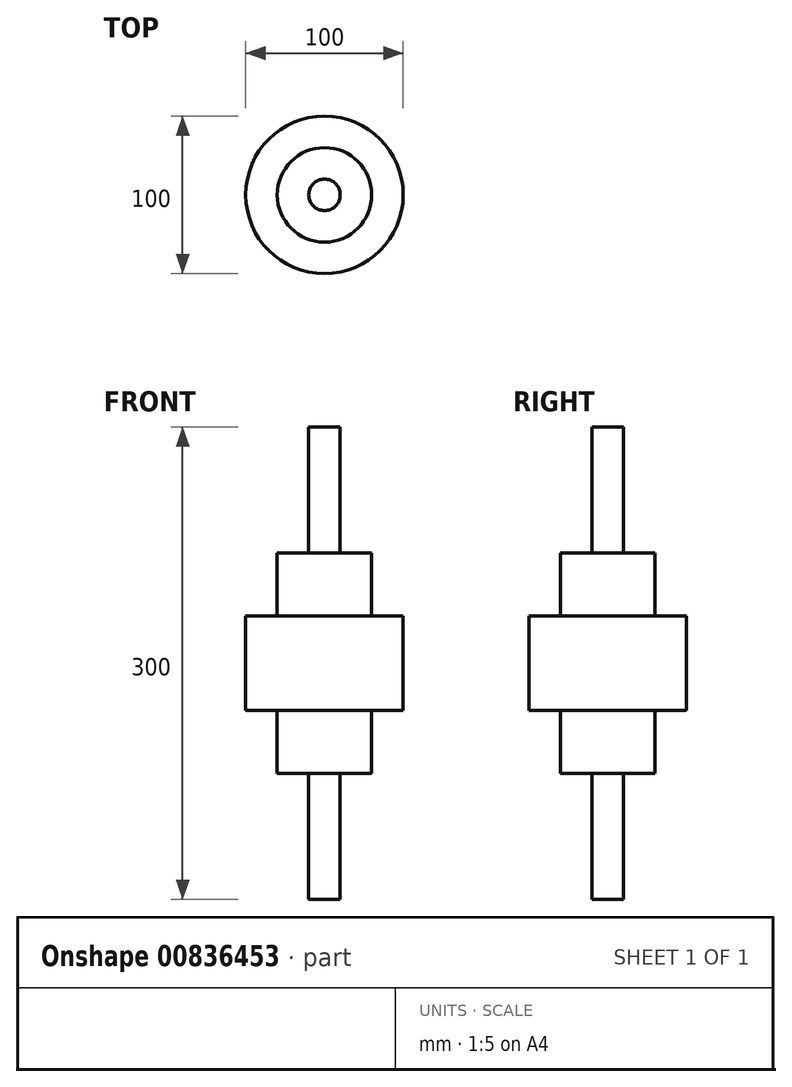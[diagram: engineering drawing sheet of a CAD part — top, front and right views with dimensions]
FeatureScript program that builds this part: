
annotation { "Feature Type Name" : "Feature", "Feature Type Description" : "" }
export const myFeature = defineFeature(function(context is Context, id is Id, definition is map)
    precondition{}
    {
        {
            var Q0;
            Q0=qCreatedBy(makeId("Top.planeOp"),FACE);
            var sketch = newSketch(context, id + "F0", { "sketchPlane" : qUnion([Q0])});
            skCircle(sketch, "E0", {"center": v(0, 0) * mm, "radius": 10 * mm});
            skSolve(sketch);
        }
        {
            var Q0;
            Q0 = qSketchRegion(id + "F0", true);
            extrude(context, id + "F1", {"entities" : qUnion([Q0]), "depth" : 80 * mm, "offsetDistance" : 25 * mm});
        }
        {
            var Q0;
            Q0=makeQuery(id+"F1.opExtrude","CAP_FACE",FACE,{"disambiguationData":[OSD([sQuery(id+"F0.wireOp",EDGE,"E0")])],"isStart":false});
            var sketch = newSketch(context, id + "F2", { "sketchPlane" : qUnion([Q0])});
            skCircle(sketch, "E1", {"center": v(0, 0) * mm, "radius": 30 * mm});
            skSolve(sketch);
        }
        {
            var Q0;
            Q0 = qSketchRegion(id + "F2", true);
            extrude(context, id + "F3", {"entities" : qUnion([Q0]), "operationType" : NewBodyOperationType.ADD, "depth" : 40 * mm, "offsetDistance" : 25 * mm});
        }
        {
            var Q0;
            Q0=makeQuery(id+"F3.opExtrude","CAP_FACE",FACE,{"disambiguationData":[OSD([sQuery(id+"F2.wireOp",EDGE,"E1")])],"isStart":false});
            var sketch = newSketch(context, id + "F4", { "sketchPlane" : qUnion([Q0])});
            skCircle(sketch, "E2", {"center": v(0, 0) * mm, "radius": 50 * mm});
            skSolve(sketch);
        }
        {
            var Q0;
            Q0 = qSketchRegion(id + "F4", true);
            extrude(context, id + "F5", {"entities" : qUnion([Q0]), "operationType" : NewBodyOperationType.ADD, "depth" : 30 * mm, "offsetDistance" : 25 * mm});
        }
        {
            var Q0;
            Q0=makeQuery(id+"F1.opExtrude","SWEPT_BODY",BODY,{"disambiguationData":[OSD([sQuery(id+"F0.wireOp",EDGE,"E0")])]});
            var Q1;
            Q1=makeQuery(id+"F5.opExtrude","CAP_FACE",FACE,{"disambiguationData":[OSD([sQuery(id+"F4.wireOp",EDGE,"E2")])],"isStart":false});
            mirror(context, id + "F6", {"operationType" : NewBodyOperationType.ADD, "entities" : qUnion([Q0]), "mirrorPlane" : qUnion([Q1])});
        }
    });
